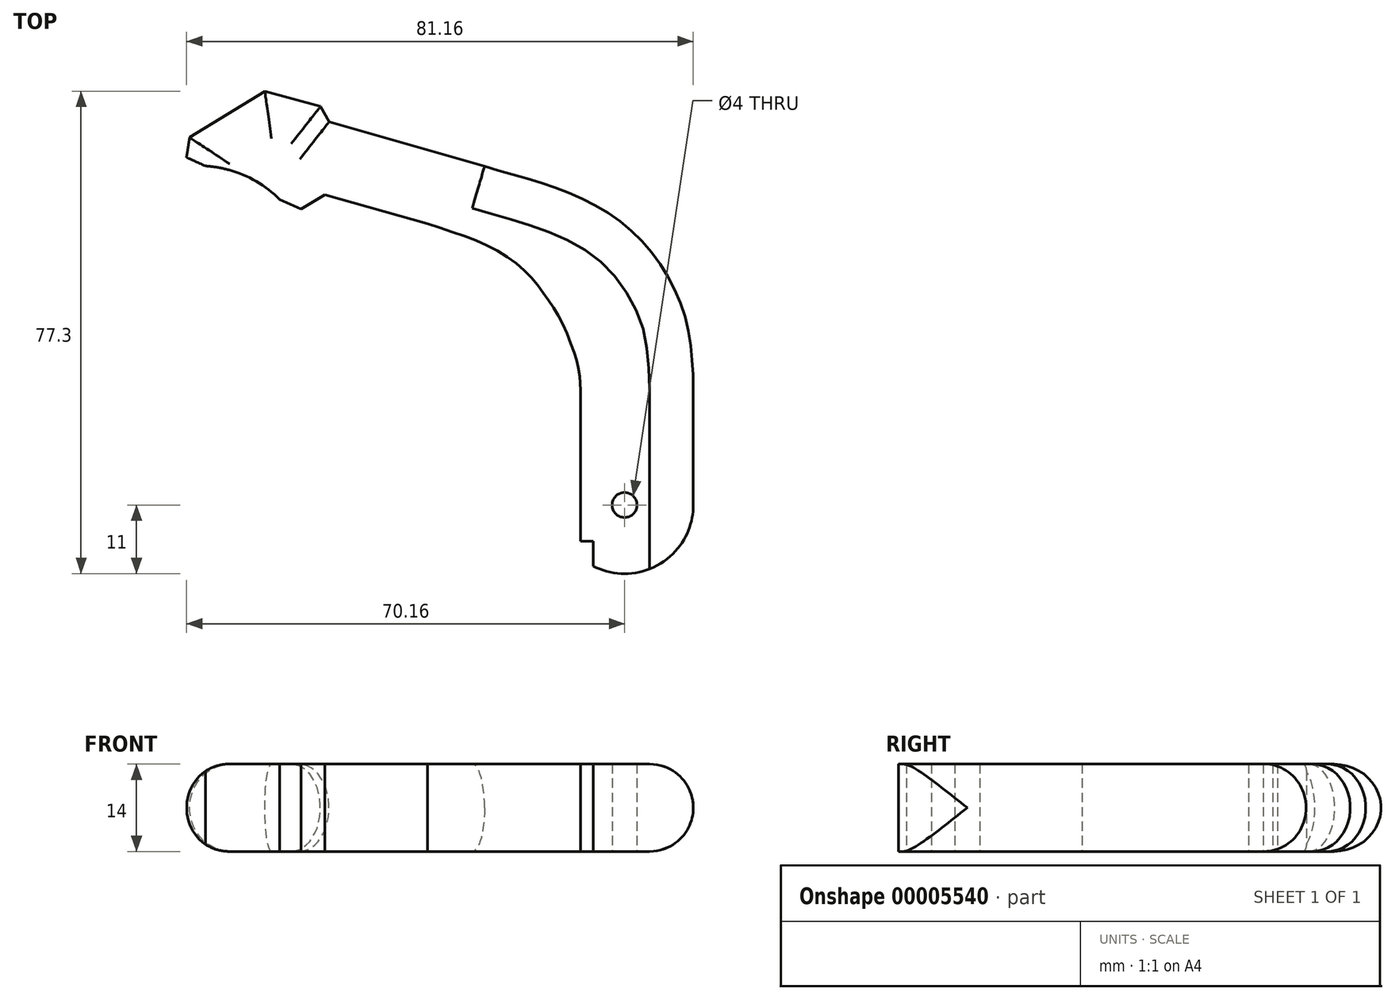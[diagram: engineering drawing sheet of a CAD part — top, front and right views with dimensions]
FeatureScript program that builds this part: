
annotation { "Feature Type Name" : "Feature", "Feature Type Description" : "" }
export const myFeature = defineFeature(function(context is Context, id is Id, definition is map)
    precondition{}
    {
        {
            var Q0;
            Q0=qCreatedBy(makeId("Top.planeOp"),FACE);
            var sketch = newSketch(context, id + "F0", { "sketchPlane" : qUnion([Q0])});
            skLineSegment(sketch, "E0", {"start": v(-80.7, 58.88) * mm, "end": v(-68.63, 66.3) * mm});
            skLineSegment(sketch, "E1", {"start": v(-68.63, 66.3) * mm, "end": v(-59.7, 63.82) * mm});
            skLineSegment(sketch, "E2", {"start": v(-59.7, 63.82) * mm, "end": v(-58.33, 61.35) * mm});
            skLineSegment(sketch, "E3", {"start": v(-58.33, 61.35) * mm, "end": v(-33.43, 54.26) * mm});
            skLineSegment(sketch, "E4", {"start": v(0, 18.5) * mm, "end": v(0, 0) * mm});
            skLineSegment(sketch, "E5", {"start": v(-80.7, 58.88) * mm, "end": v(-81.16, 55.67) * mm});
            skLineSegment(sketch, "E6", {"start": v(-81.16, 55.67) * mm, "end": v(-78.15, 54.3) * mm});
            skLineSegment(sketch, "E7", {"start": v(-62.83, 47.38) * mm, "end": v(-58.99, 49.7) * mm});
            skLineSegment(sketch, "E8", {"start": v(-58.99, 49.7) * mm, "end": v(-42.58, 45.07) * mm});
            skArc(sketch, "E9", {"start": v(-66.23, 48.91) * mm, "mid": v(-71.7, 52.7) * mm, "end": v(-78.15, 54.3) * mm});
            skFitSpline(sketch, "E10", {"points": [v(-33.43, 54.26) * mm, v(-22.87, 51.08) * mm, v(-13.66, 46.8) * mm, v(-7.33, 41.29) * mm, v(-3.55, 35.62) * mm, v(-1.17, 29.61) * mm, v(0, 18.5) * mm], "startDerivative": vector(52.87, -16) * mm, "endDerivative": vector(0, -65.68) * mm});
            skPoint(sketch, "E11.orphan", {"position": v(0, 44.75) * mm});
            skFitSpline(sketch, "E12", {"points": [v(-42.58, 45.07) * mm, v(-33.64, 41.87) * mm, v(-27.23, 37.76) * mm, v(-23.69, 33.48) * mm, v(-21.06, 29.29) * mm, v(-18.91, 23.9) * mm, v(-18.02, 18.4) * mm], "startDerivative": vector(46.77, -16.08) * mm, "endDerivative": vector(4.3, -61.62) * mm});
            skLineSegment(sketch, "E13.trimOffspring", {"start": v(-66.23, 48.91) * mm, "end": v(-62.83, 47.38) * mm});
            skPoint(sketch, "E14.orphan", {"position": v(-18.02, 0) * mm});
            skCircle(sketch, "E15", {"center": v(-11, 0) * mm, "radius": 2 * mm});
            skArc(sketch, "E16", {"start": v(-16.02, -9.79) * mm, "mid": v(-5.27, -9.39) * mm, "end": v(0, 0) * mm});
            skLineSegment(sketch, "E17", {"start": v(-18.02, 18.4) * mm, "end": v(-18.02, -5.79) * mm});
            skPoint(sketch, "E18.orphan", {"position": v(0, 0) * mm});
            skLineSegment(sketch, "E19.top", {"start": v(-18.02, -5.79) * mm, "end": v(-16.02, -5.79) * mm});
            skLineSegment(sketch, "E19.right", {"start": v(-16.02, -9.79) * mm, "end": v(-16.02, -5.79) * mm});
            skSolve(sketch);
        }
        {
            var Q0;
            Q0=makeQuery(id+"F0.imprint","IMPRINT",FACE,{"disambiguationData":[TD([[makeQuery(id+"F0.imprint","IMPRINT",EDGE,{"derivedFrom":sQuery(id+"F0.wireOp",EDGE,"E0")}),-1.0]])]});
            extrude(context, id + "F1", {"entities" : qUnion([Q0]), "depth" : 14 * mm});
        }
        {
            var Q0;
            Q0=makeQuery(id+"F1.opExtrude","CAP_EDGE",EDGE,{"disambiguationData":[OSD([sQuery(id+"F0.wireOp",EDGE,"E10")])],"isStart":false});
            var Q1;
            Q1=makeQuery(id+"F1.opExtrude","CAP_EDGE",EDGE,{"disambiguationData":[OSD([sQuery(id+"F0.wireOp",EDGE,"E10")])],"isStart":true});
            var Q2;
            Q2=makeQuery(id+"F1.opExtrude","CAP_EDGE",EDGE,{"disambiguationData":[OSD([sQuery(id+"F0.wireOp",EDGE,"E3")])],"isStart":false});
            var Q3;
            Q3=makeQuery(id+"F1.opExtrude","CAP_EDGE",EDGE,{"disambiguationData":[OSD([sQuery(id+"F0.wireOp",EDGE,"E3")])],"isStart":true});
            var Q4;
            Q4=makeQuery(id+"F1.opExtrude","CAP_EDGE",EDGE,{"disambiguationData":[OSD([sQuery(id+"F0.wireOp",EDGE,"E2")])],"isStart":false});
            var Q5;
            Q5=makeQuery(id+"F1.opExtrude","CAP_EDGE",EDGE,{"disambiguationData":[OSD([sQuery(id+"F0.wireOp",EDGE,"E2")])],"isStart":true});
            var Q6;
            Q6=makeQuery(id+"F1.opExtrude","CAP_EDGE",EDGE,{"disambiguationData":[OSD([sQuery(id+"F0.wireOp",EDGE,"E1")])],"isStart":false});
            var Q7;
            Q7=makeQuery(id+"F1.opExtrude","CAP_EDGE",EDGE,{"disambiguationData":[OSD([sQuery(id+"F0.wireOp",EDGE,"E1")])],"isStart":true});
            var Q8;
            Q8=makeQuery(id+"F1.opExtrude","CAP_EDGE",EDGE,{"disambiguationData":[OSD([sQuery(id+"F0.wireOp",EDGE,"E0")])],"isStart":true});
            var Q9;
            Q9=makeQuery(id+"F1.opExtrude","CAP_EDGE",EDGE,{"disambiguationData":[OSD([sQuery(id+"F0.wireOp",EDGE,"E0")])],"isStart":false});
            var Q10;
            Q10=makeQuery(id+"F1.opExtrude","CAP_EDGE",EDGE,{"disambiguationData":[OSD([sQuery(id+"F0.wireOp",EDGE,"E5")])],"isStart":false});
            var Q11;
            Q11=makeQuery(id+"F1.opExtrude","CAP_EDGE",EDGE,{"disambiguationData":[OSD([sQuery(id+"F0.wireOp",EDGE,"E5")])],"isStart":true});
            fillet(context, id + "F2", {"entities" : qUnion([Q0, Q1, Q2, Q3, Q4, Q5, Q6, Q7, Q8, Q9, Q10, Q11]), "radius" : 7 * mm, "allowEdgeOverflow" : false});
        }
    });
